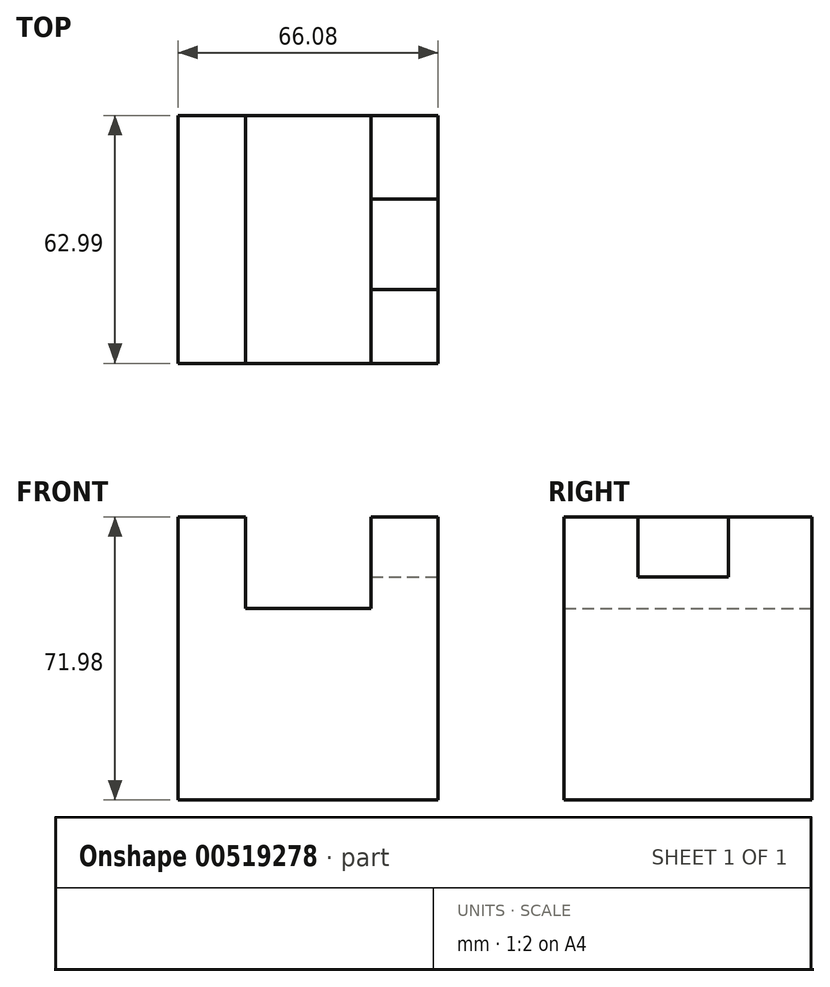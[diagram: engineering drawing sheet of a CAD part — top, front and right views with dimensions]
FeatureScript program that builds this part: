
annotation { "Feature Type Name" : "Feature", "Feature Type Description" : "" }
export const myFeature = defineFeature(function(context is Context, id is Id, definition is map)
    precondition{}
    {
        {
            var Q0;
            Q0=qCreatedBy(makeId("Front.planeOp"),FACE);
            var sketch = newSketch(context, id + "F0", { "sketchPlane" : qUnion([Q0])});
            skLineSegment(sketch, "E0.bottom", {"start": v(-33.04, 36) * mm, "end": v(-15.97, 36) * mm});
            skLineSegment(sketch, "E0.top", {"start": v(-33.04, -36) * mm, "end": v(33.04, -36) * mm});
            skLineSegment(sketch, "E0.left", {"start": v(-33.04, 36) * mm, "end": v(-33.04, -36) * mm});
            skLineSegment(sketch, "E0.right", {"start": v(33.04, 36) * mm, "end": v(33.04, -36) * mm});
            skPoint(sketch, "E0.middle", {"position": v(0, 0) * mm});
            skLineSegment(sketch, "E1.top", {"start": v(-15.97, 12.76) * mm, "end": v(15.97, 12.76) * mm});
            skLineSegment(sketch, "E1.left", {"start": v(-15.97, 36) * mm, "end": v(-15.97, 12.76) * mm});
            skLineSegment(sketch, "E1.right", {"start": v(15.97, 36) * mm, "end": v(15.97, 12.76) * mm});
            skLineSegment(sketch, "E2.trimOffspring", {"start": v(15.97, 36) * mm, "end": v(33.04, 36) * mm});
            skSolve(sketch);
        }
        {
            var Q0;
            Q0=makeQuery(id+"F0.imprint","IMPRINT",FACE,{"disambiguationData":[TD([[makeQuery(id+"F0.imprint","IMPRINT",EDGE,{"derivedFrom":sQuery(id+"F0.wireOp",EDGE,"E0.bottom")}),-1.0]])]});
            extrude(context, id + "F1", {"entities" : qUnion([Q0]), "depth" : 63 * mm, "offsetDistance" : 25.4 * mm});
        }
        {
            var Q0;
            Q0=makeQuery(id+"F1.opExtrude","SWEPT_FACE",FACE,{"disambiguationData":[OSD([sQuery(id+"F0.wireOp",EDGE,"E0.right")])]});
            var sketch = newSketch(context, id + "F2", { "sketchPlane" : qUnion([Q0])});
            skLineSegment(sketch, "E3.bottom", {"start": v(-44.19, 36) * mm, "end": v(-21.3, 36) * mm});
            skLineSegment(sketch, "E3.top", {"start": v(-44.19, 20.73) * mm, "end": v(-21.3, 20.73) * mm});
            skLineSegment(sketch, "E3.left", {"start": v(-44.19, 36) * mm, "end": v(-44.19, 20.73) * mm});
            skLineSegment(sketch, "E3.right", {"start": v(-21.3, 36) * mm, "end": v(-21.3, 20.73) * mm});
            skPoint(sketch, "E3.middle", {"position": v(-32.74, 28.36) * mm});
            skSolve(sketch);
        }
        {
            var Q0;
            Q0 = qSketchRegion(id + "F2", true);
            extrude(context, id + "F3", {"entities" : qUnion([Q0]), "operationType" : NewBodyOperationType.REMOVE, "oppositeDirection" : true, "depth" : 25.4 * mm, "offsetDistance" : 25.4 * mm});
        }
    });
